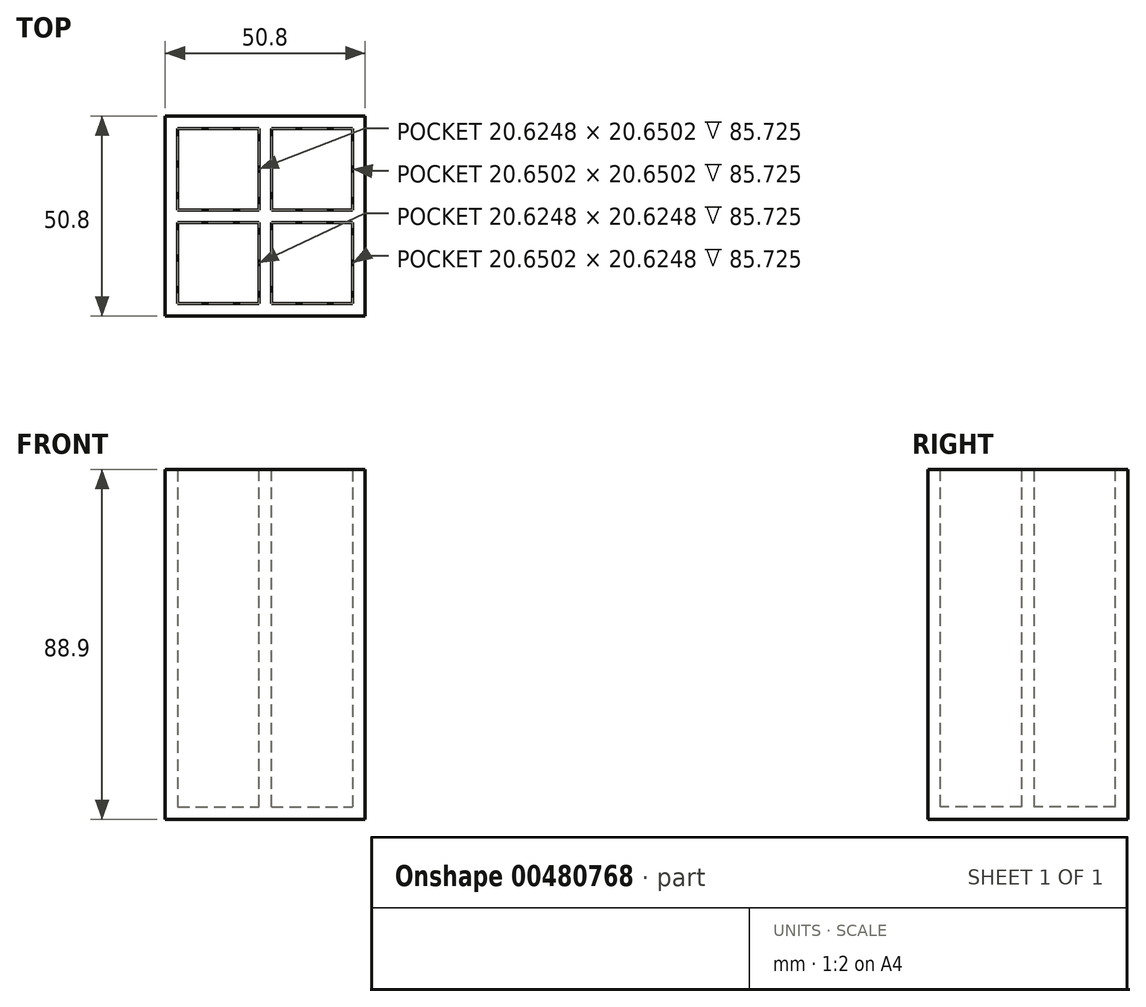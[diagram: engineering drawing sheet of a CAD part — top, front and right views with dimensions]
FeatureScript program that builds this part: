
annotation { "Feature Type Name" : "Feature", "Feature Type Description" : "" }
export const myFeature = defineFeature(function(context is Context, id is Id, definition is map)
    precondition{}
    {
        {
            var Q0;
            Q0=qCreatedBy(makeId("Top.planeOp"),FACE);
            var sketch = newSketch(context, id + "F0", { "sketchPlane" : qUnion([Q0])});
            skLineSegment(sketch, "E0.bottom", {"start": v(-25.4, 25.4) * mm, "end": v(25.4, 25.4) * mm});
            skLineSegment(sketch, "E0.top", {"start": v(-25.4, -25.4) * mm, "end": v(25.4, -25.4) * mm});
            skLineSegment(sketch, "E0.left", {"start": v(-25.4, 25.4) * mm, "end": v(-25.4, -25.4) * mm});
            skLineSegment(sketch, "E0.right", {"start": v(25.4, 25.4) * mm, "end": v(25.4, -25.4) * mm});
            skPoint(sketch, "E0.middle", {"position": v(0, 0) * mm});
            skSolve(sketch);
        }
        {
            var Q0;
            Q0 = qSketchRegion(id + "F0", true);
            extrude(context, id + "F1", {"entities" : qUnion([Q0]), "depth" : 88.9 * mm});
        }
        {
            var Q0;
            Q0=makeQuery(id+"F1.opExtrude","CAP_FACE",FACE,{"disambiguationData":[OSD([sQuery(id+"F0.wireOp",EDGE,"E0.bottom"),sQuery(id+"F0.wireOp",EDGE,"E0.top"),sQuery(id+"F0.wireOp",EDGE,"E0.left"),sQuery(id+"F0.wireOp",EDGE,"E0.right")])],"isStart":false});
            shell(context, id + "F2", {"entities" : qUnion([Q0]), "thickness" : 3.17 * mm});
        }
        {
            var Q0;
            Q0=makeQuery(id+"F1.opExtrude","CAP_FACE",FACE,{"disambiguationData":[OSD([sQuery(id+"F0.wireOp",EDGE,"E0.bottom"),sQuery(id+"F0.wireOp",EDGE,"E0.top"),sQuery(id+"F0.wireOp",EDGE,"E0.left"),sQuery(id+"F0.wireOp",EDGE,"E0.right")])],"isStart":false});
            var sketch = newSketch(context, id + "F3", { "sketchPlane" : qUnion([Q0])});
            skLineSegment(sketch, "E1.bottom", {"start": v(-1.6, 22.23) * mm, "end": v(1.57, 22.23) * mm});
            skLineSegment(sketch, "E1.top", {"start": v(-1.6, -22.23) * mm, "end": v(1.57, -22.23) * mm});
            skLineSegment(sketch, "E1.left", {"start": v(-1.6, 22.23) * mm, "end": v(-1.6, -22.23) * mm});
            skLineSegment(sketch, "E1.right", {"start": v(1.57, 22.23) * mm, "end": v(1.57, -22.23) * mm});
            skSolve(sketch);
        }
        {
            var Q0;
            Q0 = qSketchRegion(id + "F3", true);
            extrude(context, id + "F4", {"entities" : qUnion([Q0]), "oppositeDirection" : true, "depth" : 85.72 * mm});
        }
        {
            var Q0;
            Q0=makeQuery(id+"F2.opShell","OFFSET_FACE",FACE,{"disambiguationData":[OSD([sQuery(id+"F0.wireOp",EDGE,"E0.bottom"),sQuery(id+"F0.wireOp",EDGE,"E0.top"),sQuery(id+"F0.wireOp",EDGE,"E0.left"),sQuery(id+"F0.wireOp",EDGE,"E0.right")])]});
            var sketch = newSketch(context, id + "F5", { "sketchPlane" : qUnion([Q0])});
            skLineSegment(sketch, "E2.bottom", {"start": v(-22.23, 1.57) * mm, "end": v(22.23, 1.57) * mm});
            skLineSegment(sketch, "E2.top", {"start": v(-22.23, -1.6) * mm, "end": v(22.23, -1.6) * mm});
            skLineSegment(sketch, "E2.left", {"start": v(-22.23, 1.57) * mm, "end": v(-22.23, -1.6) * mm});
            skLineSegment(sketch, "E2.right", {"start": v(22.23, 1.57) * mm, "end": v(22.23, -1.6) * mm});
            skSolve(sketch);
        }
        {
            var Q0;
            Q0 = qSketchRegion(id + "F5", true);
            extrude(context, id + "F6", {"entities" : qUnion([Q0]), "operationType" : NewBodyOperationType.ADD, "depth" : 85.72 * mm});
        }
    });
